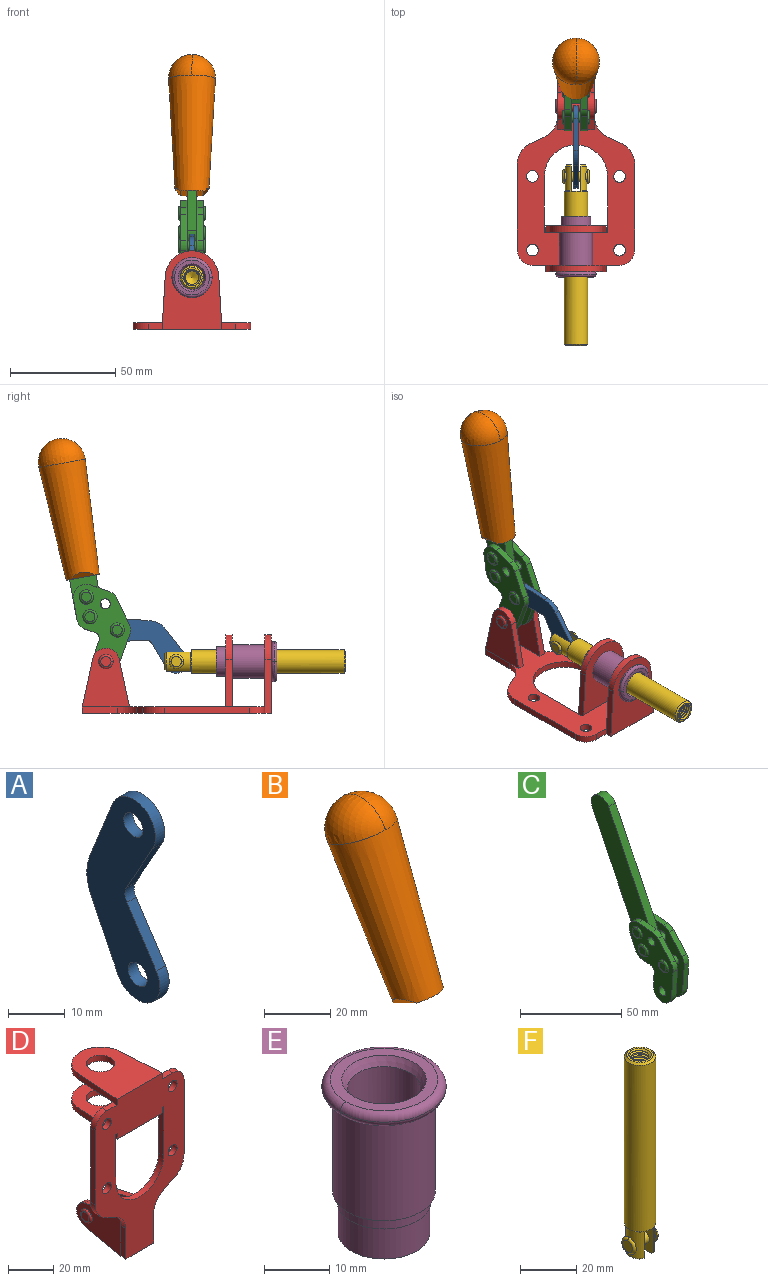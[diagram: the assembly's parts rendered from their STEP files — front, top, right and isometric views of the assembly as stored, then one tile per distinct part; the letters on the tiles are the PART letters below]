
ASSEMBLY  parts=6 mates=6
PART A: 12 faces, bbox 2.3x18.2x42.8 mm
  f0: cylinder r=2.4mm len=4.8mm, axis (1,0,0), area 34.9mm2, adj f4,f11
  f1: cylinder r=10.41mm len=8.47mm, axis (1,0,0), area 20.2mm2, adj f4,f9,f10,f11
  f2: cylinder r=3.05mm len=3.16mm, axis (1,0,0), area 7.7mm2, adj f4,f6,f7,f11
  f3: cylinder r=2.4mm len=4.8mm, axis (1,0,0), area 34.9mm2, adj f4,f11
  f4: plane 42.81x18.23mm, normal (-1,0,0), area 414.1mm2, adj f0,f1,f2,f3,f5,f6,f7,f8
  f5: cylinder r=5.54mm len=10.67mm, axis (1,0,0), area 41.8mm2, adj f4,f6,f10,f11
  f6: plane 11.66x6.53mm, normal (0,-0.87,-0.49), area 30.9mm2, adj f2,f4,f5,f11
  f7: plane 11.17x7.33mm, normal (0,-0.84,0.55), area 30.9mm2, adj f2,f4,f8,f11
  f8: cylinder r=5.54mm len=10.51mm, axis (1,0,0), area 41.8mm2, adj f4,f7,f9,f11
  f9: plane 13.67x6.67mm, normal (0,0.9,-0.44), area 35.1mm2, adj f1,f4,f8,f11
  f10: plane 14.1x5.7mm, normal (0,0.93,0.37), area 35.1mm2, adj f1,f4,f5,f11
  f11: plane 42.81x18.23mm, normal (1,0,0), area 414.1mm2, adj f0,f1,f2,f3,f5,f6,f7,f8
PART B: 11 faces, bbox 22.3x42.6x64.5 mm
  f0: sphere r=11.13mm, area 411.4mm2, adj f1,f8
  f1: cone r=11.11mm half-angle=3.3deg, axis (0,0.44,0.9), area 3251.8mm2, adj f0,f7,f8,f9,f10
  f2: cylinder r=6.16mm len=11.7mm, axis (1,0,0), area 89.5mm2, adj f3,f4,f5,f6
  f3: plane 60.23x36.75mm, normal (-1,0,0), area 763.6mm2, adj f2,f4,f6,f10
  f4: plane 51.37x25.05mm, normal (0,0.9,-0.44), area 264.2mm2, adj f2,f3,f5,f10
  f5: plane 60.23x36.75mm, normal (1,0,0), area 763.6mm2, adj f2,f4,f6,f10
  f6: plane 51.37x25.05mm, normal (0,-0.9,0.44), area 264.2mm2, adj f2,f3,f5,f10
  f7: plane 9.95x5.95mm, normal (0.71,-0.31,-0.64), area 25.8mm2, adj f1,f10
  f8: sphere r=11.13mm, area 411.4mm2, adj f0,f1
  f9: plane 9.95x5.95mm, normal (-0.71,-0.31,-0.64), area 25.8mm2, adj f1,f10
  f10: plane 14.27x11.38mm, normal (0,-0.44,-0.9), area 106.7mm2, adj f1,f3,f4,f5,f6,f7,f9
PART C: 59 faces, bbox 12.9x60.2x99.6 mm
  f0: torus R=2.39mm, axis (-1,0,0), area 14.9mm2, adj f20,f43,f51
  f1: torus R=2.39mm, axis (-1,0,0), area 14.9mm2, adj f19,f42,f51
  f2: torus R=2.39mm, axis (-1,0,0), area 14.9mm2, adj f18,f35,f51
  f3: torus R=2.39mm, axis (-1,0,0), area 14.9mm2, adj f14,f17,f23
  f4: torus R=2.39mm, axis (-1,0,0), area 14.9mm2, adj f13,f16,f23
  f5: torus R=2.39mm, axis (-1,0,0), area 14.9mm2, adj f12,f15,f23
  f6: cylinder r=2.39mm len=4.78mm, axis (1,0,0), area 46.5mm2, adj f48,f50,f51
  f7: cylinder r=2.39mm len=4.78mm, axis (1,0,0), area 46.5mm2, adj f50,f51
  f8: cylinder r=6.35mm len=12.68mm, axis (1,0,0), area 61.8mm2, adj f38,f39,f50,f51
  f9: cylinder r=2.39mm len=4.78mm, axis (-1,0,0), area 70.5mm2, adj f46,f50
  f10: cylinder r=2.39mm len=4.78mm, axis (-1,0,0), area 46.5mm2, adj f23,f45,f46
  f11: cylinder r=2.39mm len=4.78mm, axis (-1,0,0), area 46.5mm2, adj f23,f46
  f12: plane 4.78x4.78mm, normal (1,0,0), area 17.9mm2, adj f5,f15
  f13: plane 4.78x4.78mm, normal (1,0,0), area 17.9mm2, adj f4,f16
  f14: plane 4.78x4.78mm, normal (1,0,0), area 17.9mm2, adj f3,f17
  f15: torus R=2.39mm, axis (-1,0,0), area 14.9mm2, adj f5,f12,f23
  f16: torus R=2.39mm, axis (-1,0,0), area 14.9mm2, adj f4,f13,f23
  f17: torus R=2.39mm, axis (-1,0,0), area 14.9mm2, adj f3,f14,f23
  f18: plane 4.78x4.78mm, normal (-1,0,0), area 17.9mm2, adj f2,f35
  f19: plane 4.78x4.78mm, normal (-1,0,0), area 17.9mm2, adj f1,f42
  f20: plane 4.78x4.78mm, normal (-1,0,0), area 17.9mm2, adj f0,f43
  f21: plane 2.26x0.2mm, normal (1,0,0), area 0.2mm2, adj f31,f44
  f22: plane 2.26x0.2mm, normal (-1,0,0), area 0.2mm2, adj f41,f44
  f23: plane 39.37x30.77mm, normal (1,0,0), area 565.5mm2, adj f3,f4,f5,f10,f11,f15,f16,f17
  f24: cylinder r=6.1mm len=4.15mm, axis (-1,0,0), area 14.7mm2, adj f23,f25,f32,f46
  f25: plane 10.25x9.01mm, normal (0,-0.75,0.66), area 42.3mm2, adj f23,f24,f26,f46
  f26: cylinder r=6.35mm len=4.64mm, axis (-1,0,0), area 15.6mm2, adj f23,f25,f27,f46
  f27: plane 15.84x3.1mm, normal (0,-1,-0.07), area 49.2mm2, adj f23,f26,f28,f46
  f28: cylinder r=6.35mm len=12.68mm, axis (-1,0,0), area 61.8mm2, adj f23,f27,f29,f46
  f29: plane 8.11x3.1mm, normal (0,1,0.07), area 25.2mm2, adj f23,f28,f30,f46
  f30: cylinder r=3.05mm len=3.25mm, axis (-1,0,0), area 14.8mm2, adj f23,f29,f31,f46
  f31: plane 5.99x3.1mm, normal (0,0.07,-1), area 18.6mm2, adj f21,f23,f30,f44,f46
  f32: plane 9.5x3.1mm, normal (0,-0.07,1), area 29.5mm2, adj f23,f24,f33,f46,f47
  f33: cylinder r=6.1mm len=8.63mm, axis (-1,0,0), area 39.1mm2, adj f23,f32,f34,f47
  f34: plane 8.65x3.96mm, normal (0,0.91,-0.42), area 29.5mm2, adj f23,f33,f44,f47
  f35: torus R=2.39mm, axis (-1,0,0), area 14.9mm2, adj f2,f18,f51
  f36: plane 10.25x9.01mm, normal (0,-0.75,0.66), area 42.3mm2, adj f37,f49,f50,f51
  f37: cylinder r=6.35mm len=4.64mm, axis (1,0,0), area 15.6mm2, adj f36,f38,f50,f51
  f38: plane 15.84x3.1mm, normal (0,-1,-0.07), area 49.2mm2, adj f8,f37,f50,f51
  f39: plane 8.11x3.1mm, normal (0,1,0.07), area 25.2mm2, adj f8,f40,f50,f51
  f40: cylinder r=3.05mm len=3.25mm, axis (1,0,0), area 14.8mm2, adj f39,f41,f50,f51
  f41: plane 5.99x3.1mm, normal (0,0.07,-1), area 18.6mm2, adj f22,f40,f44,f50,f51
  f42: torus R=2.39mm, axis (-1,0,0), area 14.9mm2, adj f1,f19,f51
  f43: torus R=2.39mm, axis (-1,0,0), area 14.9mm2, adj f0,f20,f51
  f44: cylinder r=6.35mm len=12.12mm, axis (-1,0,0), area 128.9mm2, adj f21,f22,f23,f31,f34,f41,f46,f47
  f45: plane 2.65x1.35mm, normal (1,0,0), area 1mm2, adj f10,f55
  f46: plane 39.08x20.42mm, normal (-1,0,0), area 412.5mm2, adj f9,f10,f11,f24,f25,f26,f27,f28
  f47: plane 77.62x39.82mm, normal (1,0,0), area 850mm2, adj f32,f33,f34,f44,f53,f54,f55
  f48: plane 2.65x1.35mm, normal (-1,0,0), area 1mm2, adj f6,f55
  f49: cylinder r=6.1mm len=4.15mm, axis (1,0,0), area 14.7mm2, adj f36,f50,f51,f56
  f50: plane 39.08x20.42mm, normal (1,0,0), area 412.5mm2, adj f6,f7,f8,f9,f36,f37,f38,f39
  f51: plane 39.37x30.77mm, normal (-1,0,0), area 565.5mm2, adj f0,f1,f2,f6,f7,f8,f35,f36
  f52: plane 8.65x3.96mm, normal (0,0.91,-0.42), area 29.5mm2, adj f44,f51,f57,f58
  f53: plane 68.49x33.4mm, normal (0,0.9,-0.44), area 358.1mm2, adj f44,f47,f54,f58
  f54: cylinder r=6.35mm len=12.06mm, axis (1,0,0), area 93.7mm2, adj f47,f53,f55,f58
  f55: plane 68.49x33.4mm, normal (0,-0.9,0.44), area 358.1mm2, adj f44,f45,f46,f47,f48,f50,f54,f58
  f56: plane 9.5x3.1mm, normal (0,-0.07,1), area 29.5mm2, adj f49,f50,f51,f57,f58
  f57: cylinder r=6.1mm len=8.63mm, axis (1,0,0), area 39.1mm2, adj f51,f52,f56,f58
  f58: plane 77.62x39.82mm, normal (-1,0,0), area 850mm2, adj f44,f52,f53,f54,f55,f56,f57
PART D: 55 faces, bbox 55.7x37.4x89.8 mm
  f0: torus R=2.41mm, axis (-1,0,0), area 15mm2, adj f11,f15,f25
  f1: torus R=2.41mm, axis (-1,0,0), area 15mm2, adj f10,f12,f22
  f2: cylinder r=2.78mm len=5.56mm, axis (0,-1,0), area 54.2mm2, adj f30,f54
  f3: cylinder r=14.99mm len=29.97mm, axis (0,-1,0), area 145.9mm2, adj f30,f49,f53,f54
  f4: cylinder r=2.78mm len=5.56mm, axis (0,-1,0), area 54.2mm2, adj f30,f54
  f5: cylinder r=2.78mm len=5.56mm, axis (0,-1,0), area 54.2mm2, adj f30,f54
  f6: cylinder r=2.78mm len=5.56mm, axis (0,-1,0), area 54.2mm2, adj f30,f54
  f7: cylinder r=6.35mm len=12.7mm, axis (0,0,1), area 123.6mm2, adj f27,f51
  f8: cylinder r=6.35mm len=12.7mm, axis (0,0,-1), area 124.7mm2, adj f21,f35
  f9: cylinder r=2.41mm len=11.18mm, axis (-1,0,0), area 169.4mm2, adj f16,f19
  f10: plane 4.83x4.83mm, normal (1,0,0), area 18.3mm2, adj f1,f12
  f11: plane 4.83x4.83mm, normal (-1,0,0), area 18.3mm2, adj f0,f15
  f12: torus R=2.41mm, axis (-1,0,0), area 15mm2, adj f1,f10,f22
  f13: cylinder r=6.35mm len=12.41mm, axis (1,0,0), area 53.4mm2, adj f18,f19,f22,f23
  f14: cylinder r=6.35mm len=12.41mm, axis (-1,0,0), area 53.4mm2, adj f16,f17,f24,f25
  f15: torus R=2.41mm, axis (-1,0,0), area 15mm2, adj f0,f11,f25
  f16: plane 27.86x22.35mm, normal (1,0,0), area 425.4mm2, adj f9,f14,f17,f24,f30
  f17: plane 22.86x4.97mm, normal (0,0.21,0.98), area 72.5mm2, adj f14,f16,f25,f30
  f18: plane 22.86x4.97mm, normal (0,0.21,0.98), area 72.5mm2, adj f13,f19,f22,f30
  f19: plane 27.86x22.35mm, normal (-1,0,0), area 425.4mm2, adj f9,f13,f18,f23,f30
  f20: cylinder r=12.7mm len=25.35mm, axis (0,0,-1), area 119.8mm2, adj f21,f34,f35,f36
  f21: plane 34.21x28.07mm, normal (0,0,-1), area 702.4mm2, adj f8,f20,f30,f34,f36
  f22: plane 27.96x22.45mm, normal (1,0,0), area 407.2mm2, adj f1,f12,f13,f18,f23,f30,f42,f43
  f23: plane 22.86x4.97mm, normal (0,0.21,-0.98), area 72.5mm2, adj f13,f19,f22,f44
  f24: plane 22.86x4.97mm, normal (0,0.21,-0.98), area 72.5mm2, adj f14,f16,f25,f44
  f25: plane 27.86x22.35mm, normal (-1,0,0), area 407.1mm2, adj f0,f14,f15,f17,f24,f30,f45,f46
  f26: plane 3.1x0.95mm, normal (0,0,-1), area 2.7mm2, adj f30,f49,f50,f54
  f27: plane 34.21x28.07mm, normal (0,0,1), area 702.4mm2, adj f7,f28,f30,f50,f52
  f28: cylinder r=12.7mm len=25.35mm, axis (0,0,1), area 118.8mm2, adj f27,f50,f51,f52
  f29: plane 3.1x0.95mm, normal (0,0,-1), area 2.7mm2, adj f30,f52,f53,f54
  f30: plane 86.54x55.63mm, normal (0,1,0), area 2362.9mm2, adj f2,f3,f4,f5,f6,f16,f17,f18
  f31: plane 40.56x3.1mm, normal (-1,0,0), area 125.7mm2, adj f30,f32,f48,f54
  f32: cylinder r=7.11mm len=7.11mm, axis (0,-1,0), area 34.6mm2, adj f30,f31,f33,f54
  f33: plane 6.67x3.1mm, normal (0,0,1), area 20.4mm2, adj f30,f32,f34,f54
  f34: plane 25.39x3.13mm, normal (-1,0.06,0), area 79.5mm2, adj f20,f21,f33,f35,f54
  f35: plane 37.31x28.45mm, normal (0,0,1), area 789.9mm2, adj f8,f20,f34,f36,f54
  f36: plane 25.39x3.13mm, normal (1,0.06,0), area 79.5mm2, adj f20,f21,f35,f37,f54
  f37: plane 6.67x3.1mm, normal (0,0,1), area 20.4mm2, adj f30,f36,f38,f54
  f38: cylinder r=7.11mm len=7.11mm, axis (0,-1,0), area 34.6mm2, adj f30,f37,f39,f54
  f39: plane 40.56x3.1mm, normal (1,0,0), area 125.7mm2, adj f30,f38,f40,f54
  f40: cylinder r=11.18mm len=10.16mm, axis (0,-1,0), area 39.5mm2, adj f30,f39,f41,f54
  f41: plane 6.09x3.1mm, normal (0.42,0,-0.91), area 20.8mm2, adj f30,f40,f42,f54
  f42: cylinder r=11.18mm len=9.41mm, axis (0,-1,0), area 37.2mm2, adj f22,f30,f41,f43,f54
  f43: plane 16.5x3.1mm, normal (1,0,0), area 51.1mm2, adj f22,f42,f44,f54
  f44: plane 17.37x3.1mm, normal (0,0,-1), area 53.8mm2, adj f23,f24,f30,f43,f45,f54
  f45: plane 16.5x3.1mm, normal (-1,0,0), area 51.1mm2, adj f25,f44,f46,f54
  f46: cylinder r=11.18mm len=9.41mm, axis (0,-1,0), area 37.2mm2, adj f25,f30,f45,f47,f54
  f47: plane 6.09x3.1mm, normal (-0.42,0,-0.91), area 20.8mm2, adj f30,f46,f48,f54
  f48: cylinder r=11.18mm len=10.16mm, axis (0,-1,0), area 39.5mm2, adj f30,f31,f47,f54
  f49: plane 26.54x3.1mm, normal (-1,0,0), area 82.3mm2, adj f3,f26,f30,f54
  f50: plane 25.39x3.1mm, normal (1,0.06,0), area 78.8mm2, adj f26,f27,f28,f51,f54
  f51: plane 37.31x28.45mm, normal (0,0,-1), area 789.9mm2, adj f7,f28,f50,f52,f54
  f52: plane 25.39x3.1mm, normal (-1,0.06,0), area 78.8mm2, adj f27,f28,f29,f51,f54
  f53: plane 26.54x3.1mm, normal (1,0,0), area 82.3mm2, adj f3,f29,f30,f54
  f54: plane 89.66x55.63mm, normal (0,-1,0), area 2678.5mm2, adj f2,f3,f4,f5,f6,f26,f29,f31
PART E: 15 faces, bbox 20.6x20.6x28.7 mm
  f0: torus R=8.26mm, axis (0,0,1), area 56.8mm2, adj f1,f10,f12
  f1: torus R=8.26mm, axis (0,0,1), area 56.8mm2, adj f0,f6,f13
  f2: cylinder r=5.59mm len=25.91mm, axis (0,0,1), area 909.6mm2, adj f3,f4
  f3: cone r=6.86mm half-angle=45deg, axis (0,0,-1), area 70.2mm2, adj f2,f14
  f4: cone r=6.47mm half-angle=30deg, axis (0,0,1), area 66.7mm2, adj f2,f13
  f5: cylinder r=7.04mm len=14.07mm, axis (0,0,1), area 252.6mm2, adj f11,f14
  f6: torus R=8.26mm, axis (0,0,1), area 56.8mm2, adj f1,f12,f13
  f7: cylinder r=7.16mm len=14.33mm, axis (0,0,1), area 91.5mm2, adj f9,f11
  f8: cylinder r=7.86mm len=18.42mm, axis (0,0,1), area 909.6mm2, adj f9,f10
  f9: plane 15.72x15.72mm, normal (0,0,-1), area 33mm2, adj f7,f8
  f10: plane 16.51x16.51mm, normal (0,0,-1), area 19.9mm2, adj f0,f8,f12
  f11: plane 14.33x14.33mm, normal (0,0,-1), area 5.7mm2, adj f5,f7
  f12: torus R=8.26mm, axis (0,0,1), area 56.8mm2, adj f0,f6,f10
  f13: plane 16.51x16.51mm, normal (0,0,1), area 82.7mm2, adj f1,f4,f6
  f14: plane 14.07x14.07mm, normal (0,0,-1), area 7.8mm2, adj f3,f5
PART F: 48 faces, bbox 12.6x11.1x86.1 mm
  f0: torus R=2.41mm, axis (-1,0,0), area 15mm2, adj f30,f32,f34
  f1: torus R=2.41mm, axis (-1,0,0), area 15mm2, adj f29,f31,f33
  f2: cylinder r=5.54mm len=72.39mm, axis (0,0,1), area 2518.5mm2, adj f3,f4,f42,f43
  f3: cone r=5.54mm half-angle=45deg, axis (0,0,1), area 7.6mm2, adj f2,f5,f41
  f4: cone r=5.54mm half-angle=45deg, axis (0,0,-1), area 34.9mm2, adj f2,f39
  f5: cylinder r=5.08mm len=11.48mm, axis (0,0,1), area 108.3mm2, adj f3,f7,f8,f41
  f6: cylinder r=2.41mm len=4.83mm, axis (-1,0,0), area 71.2mm2, adj f40,f41
  f7: cylinder r=2.41mm len=4.83mm, axis (-1,0,0), area 7.6mm2, adj f5,f34
  f8: cone r=5.08mm half-angle=45deg, axis (0,0,1), area 10.6mm2, adj f5,f37,f41
  f9: cone r=3.98mm half-angle=45deg, axis (0,0,1), area 17.6mm2, adj f27,f39,f45,f46,f47
  f10: cylinder r=2.41mm len=4.83mm, axis (-1,0,0), area 7.6mm2, adj f33,f38
  f11: cylinder r=3.2mm len=6.4mm, axis (0,0,1), area 78.4mm2, adj f12,f28,f44,f45,f47
  f12: cylinder r=3.2mm len=6.4mm, axis (0,0,1), area 10.5mm2, adj f11,f13,f45,f47
  f13: cylinder r=3.2mm len=6.4mm, axis (0,0,1), area 10.5mm2, adj f12,f14,f45,f47
  f14: cylinder r=3.2mm len=6.4mm, axis (0,0,1), area 10.5mm2, adj f13,f15,f45,f47
  f15: cylinder r=3.2mm len=6.4mm, axis (0,0,1), area 10.5mm2, adj f14,f16,f45,f47
  f16: cylinder r=3.2mm len=6.4mm, axis (0,0,1), area 10.5mm2, adj f15,f17,f45,f47
  f17: cylinder r=3.2mm len=6.4mm, axis (0,0,1), area 10.5mm2, adj f16,f18,f45,f47
  f18: cylinder r=3.2mm len=6.4mm, axis (0,0,1), area 10.5mm2, adj f17,f19,f45,f47
  f19: cylinder r=3.2mm len=6.4mm, axis (0,0,1), area 10.5mm2, adj f18,f20,f45,f47
  f20: cylinder r=3.2mm len=6.4mm, axis (0,0,1), area 10.5mm2, adj f19,f21,f45,f47
  f21: cylinder r=3.2mm len=6.4mm, axis (0,0,1), area 10.5mm2, adj f20,f22,f45,f47
  f22: cylinder r=3.2mm len=6.4mm, axis (0,0,1), area 10.5mm2, adj f21,f23,f45,f47
  f23: cylinder r=3.2mm len=6.4mm, axis (0,0,1), area 10.5mm2, adj f22,f24,f45,f47
  f24: cylinder r=3.2mm len=6.4mm, axis (0,0,1), area 10.5mm2, adj f23,f25,f45,f47
  f25: cylinder r=3.2mm len=6.4mm, axis (0,0,1), area 10.5mm2, adj f24,f26,f45,f47
  f26: cylinder r=3.2mm len=6.4mm, axis (0,0,1), area 10.5mm2, adj f25,f27,f45,f47
  f27: cylinder r=3.2mm len=6.4mm, axis (0,0,1), area 7.4mm2, adj f9,f26,f45,f47
  f28: cone r=3.2mm half-angle=60deg, axis (0,0,1), area 37.2mm2, adj f11
  f29: plane 4.83x4.83mm, normal (-1,0,0), area 18.3mm2, adj f1,f31
  f30: plane 4.83x4.83mm, normal (1,0,0), area 18.3mm2, adj f0,f32
  f31: torus R=2.41mm, axis (-1,0,0), area 15mm2, adj f1,f29,f33
  f32: torus R=2.41mm, axis (-1,0,0), area 15mm2, adj f0,f30,f34
  f33: plane 6.83x6.83mm, normal (1,0,0), area 18.3mm2, adj f1,f10,f31
  f34: plane 6.83x6.83mm, normal (-1,0,0), area 18.3mm2, adj f0,f7,f32
  f35: cone r=5.08mm half-angle=45deg, axis (0,0,1), area 10.6mm2, adj f36,f38,f40
  f36: plane 7.25x1.97mm, normal (0,0,-1), area 10mm2, adj f35,f40
  f37: plane 7.25x1.97mm, normal (0,0,-1), area 10mm2, adj f8,f41
  f38: cylinder r=5.08mm len=11.48mm, axis (0,0,1), area 108.3mm2, adj f10,f35,f40,f42
  f39: plane 9.55x9.55mm, normal (0,0,1), area 22mm2, adj f4,f9
  f40: plane 12.76x10.09mm, normal (1,0,0), area 95.7mm2, adj f6,f35,f36,f38,f42,f43
  f41: plane 12.76x10.09mm, normal (-1,0,0), area 95.7mm2, adj f3,f5,f6,f8,f37,f43
  f42: cone r=5.54mm half-angle=45deg, axis (0,0,1), area 7.6mm2, adj f2,f38,f40
  f43: plane 11.07x4.7mm, normal (0,0,-1), area 50.4mm2, adj f2,f40,f41
  f44: plane 0.89x0.62mm, normal (-1,0,0), area 0.3mm2, adj f11,f45,f46,f47
  f45: bspline ~24.8x7.63mm, area 266.6mm2, adj f9,f11,f12,f13,f14,f15,f16,f17
  f46: bspline ~24.87x7.63mm, area 73.6mm2, adj f9,f44,f45,f47
  f47: bspline ~24.98x7.63mm, area 272.5mm2, adj f9,f11,f12,f13,f14,f15,f16,f17
PLACE A rot(axis=(1,0,0),120.1deg) t=(0,33.59,11.07)mm
PLACE B rot(axis=(1,0,0),15.7deg) t=(0,8.85,48.84)mm
PLACE C rot(axis=(1,0,0),15.7deg) t=(0,8.85,48.84)mm
PLACE D rot(axis=(1,0,0),90deg) t=(0,9.14,0)mm fixed
PLACE E rot(axis=(1,0,0),90deg) t=(0,9.14,0)mm
PLACE F rot(axis=(1,0,0),90deg) t=(0,23.34,0)mm
MATE revolute A.f5 <-> F.f6  axis (1,0,0) through (0,7.87,24.61)mm
MATE fastened C.f54 <-> B.f2  axis (1,0,0) through (0,62.41,120.8)mm
MATE revolute A.f3 <-> C.f4  axis (1,0,0) through (0,35.88,39.56)mm
MATE revolute D.f0 <-> C.f7  axis (-1,0,0) through (0,41.23,24.61)mm
MATE slider F.f2 <-> D.f7  axis (0,-1,0) through (0,-35.44,24.61)mm
MATE fastened D.f7 <-> E.f0  axis (0,-1,0) through (0,-37.25,24.61)mm
